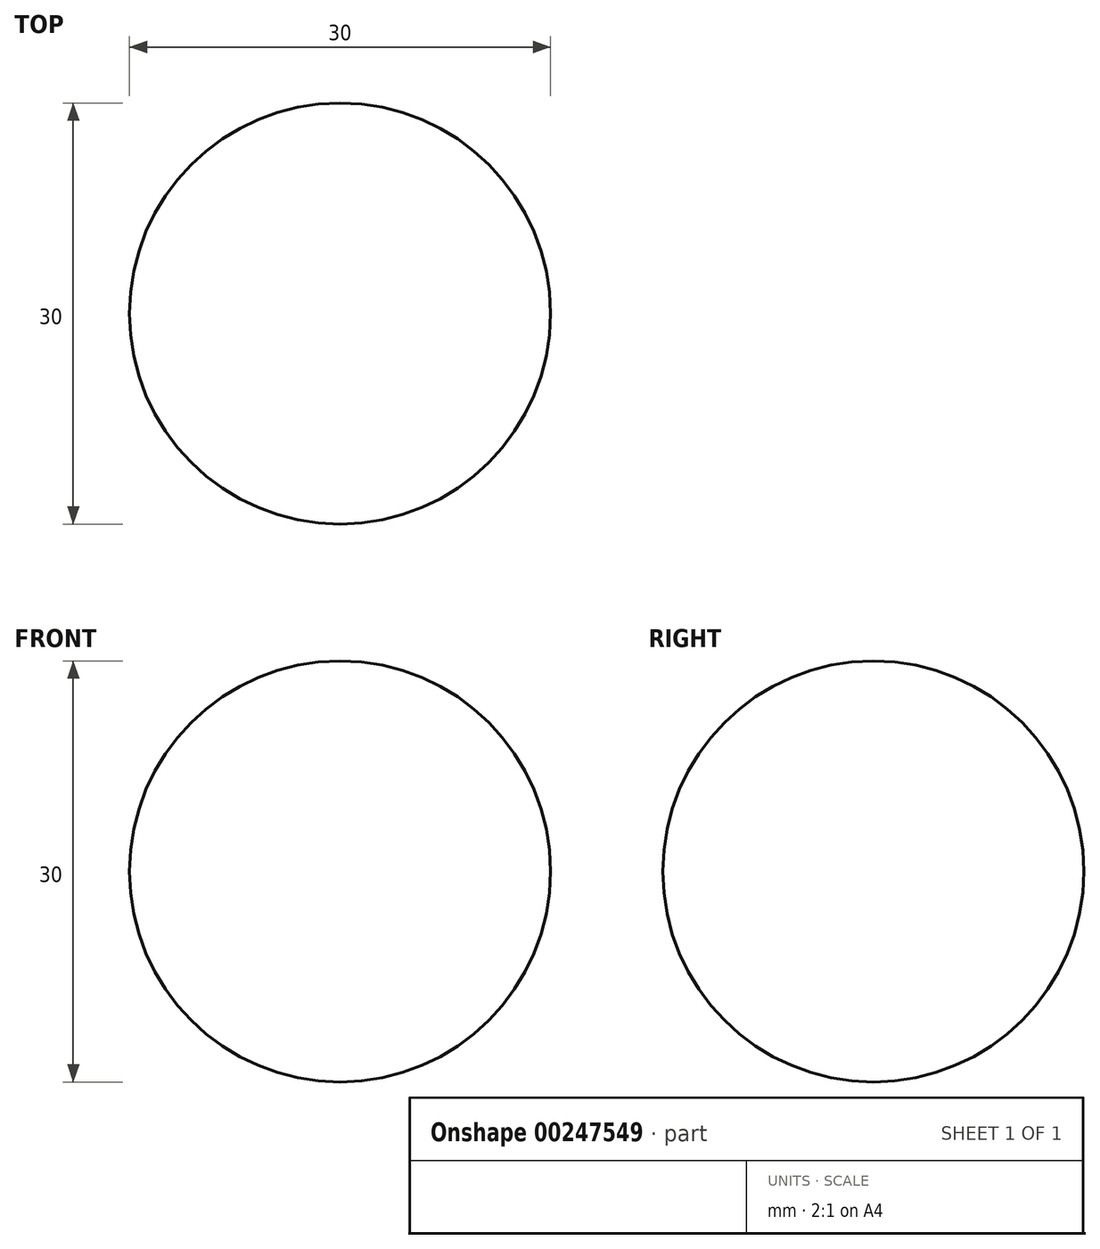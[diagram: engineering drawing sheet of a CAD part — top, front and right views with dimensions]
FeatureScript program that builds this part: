
annotation { "Feature Type Name" : "Feature", "Feature Type Description" : "" }
export const myFeature = defineFeature(function(context is Context, id is Id, definition is map)
    precondition{}
    {
        {
            var Q0;
            Q0=qCreatedBy(makeId("Top.planeOp"),FACE);
            var sketch = newSketch(context, id + "F0", { "sketchPlane" : qUnion([Q0])});
            skCircle(sketch, "E0", {"center": v(0, 0) * mm, "radius": 15 * mm});
            skLineSegment(sketch, "E1", {"start": v(-15, 0) * mm, "end": v(15, 0) * mm});
            skSolve(sketch);
        }
        {
            var Q0;
            {var subQ0=sQuery(id+"F0.wireOp",EDGE,"E1");Q0=makeQuery(id+"F0.imprint","IMPRINT",FACE,{"disambiguationData":[TD([[makeQuery(id+"F0.imprint","IMPRINT",EDGE,{"derivedFrom":subQ0}),1.0]])]});}
            var Q1;
            Q1=sQuery(id+"F0.wireOp",EDGE,"E1");
            revolve(context, id + "F1", {"entities" : qUnion([Q0]), "axis" : qUnion([Q1]), "revolveType" : RevolveType.FULL});
        }
    });
